# Revit family: EURS_63_LF_FB_ST321Y
name_source: partatom
category: Lighting Fixtures
revit_build: Autodesk Revit 2018 (Build: 20190510_1515(x64)
units: mm (PartAtom-declared; Revit-internal decimal feet)

## family parameters
Cut with Voids When Loaded = No
Host = Face
Light Source = No
Part Type = Normal
Room Calculation Point = No
Round Connector Dimension = Use Diameter
Shared = No

## types (1)
- Type catalog
    12NC = 12NC CODE
    Apparent Load = 0 VA
    BIM Library - URL = http://www.lighting.philips.com
    Ceiling thickness = 13 mm  [stored 0.0426509 ft]
    Content modified date = DATE
    Content version = 1.0
    Default Elevation = 0 mm  [stored 0 ft]
    Description = MODEL NAME
    EOC = EOC CODE
    ETIM code = MODEL ETIM CODE
    ETIM code URL = ETIM CODE WEBPAGE
    Fixture code = FIXTURE CODE
    Hanger distance = 327 mm
    Height = 100 mm  [stored 0.328084 ft]
    Lamp = LAMP NAME
    Lamp type = ST321Y IES Data : 1 xLED17S_827 HMB
    Last IES update = DATE
    Length = 70 mm  [stored 0.229659 ft]
    Light source = 2 mm  [stored 0.00656168 ft]
    Manufacturer = Philips
    Model = MODEL NUMBER
    Order code = ORDER CODE
    Product catalog - URL = MODEL WEBPAGE
    Suspension height = 100 mm  [stored 0.328084 ft]
    Type Comments = Pendant
    URL = http://www.lighting.philips.com
    Voltage (V) = 230 V
    Width = 565 mm  [stored 1.85367 ft]

note: [stored X ft] marks values corroborated as IEEE doubles in the binary element streams (Revit-internal decimal feet)

## geometry (parser evidence)
native form markers: Blend x5, Sweep x58
no freeform markers — native parametric forms only
